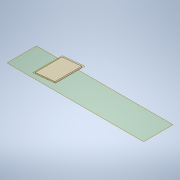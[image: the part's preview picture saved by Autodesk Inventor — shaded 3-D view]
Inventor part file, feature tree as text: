
AUTODESK INVENTOR PART (.ipt)
format: ipt  version: 2020.2 (Build 242310000, 310)  size: 124,928 bytes
history: native  units: mm
features: extrude x3, sketch x3, other x2
ambient origin geometry x8: Origin, YZ Plane, XZ Plane, XY Plane, X Axis, Y Axis, Z Axis, Center Point
bodies: Solide1 (feature_tree)
feature tree (8):
  extrude  "Extrusion1"  Depth=785.7mm
  other  "Plan de construction1"
  extrude  "Extrusion2"  Depth=3.0mm
  other  "Plan de construction2"
  extrude  "Extrusion3"  Depth=65.0mm TaperAngle=0.0deg
  sketch  "Esquisse1"
  sketch  "Esquisse2"
  sketch  "Esquisse3"
